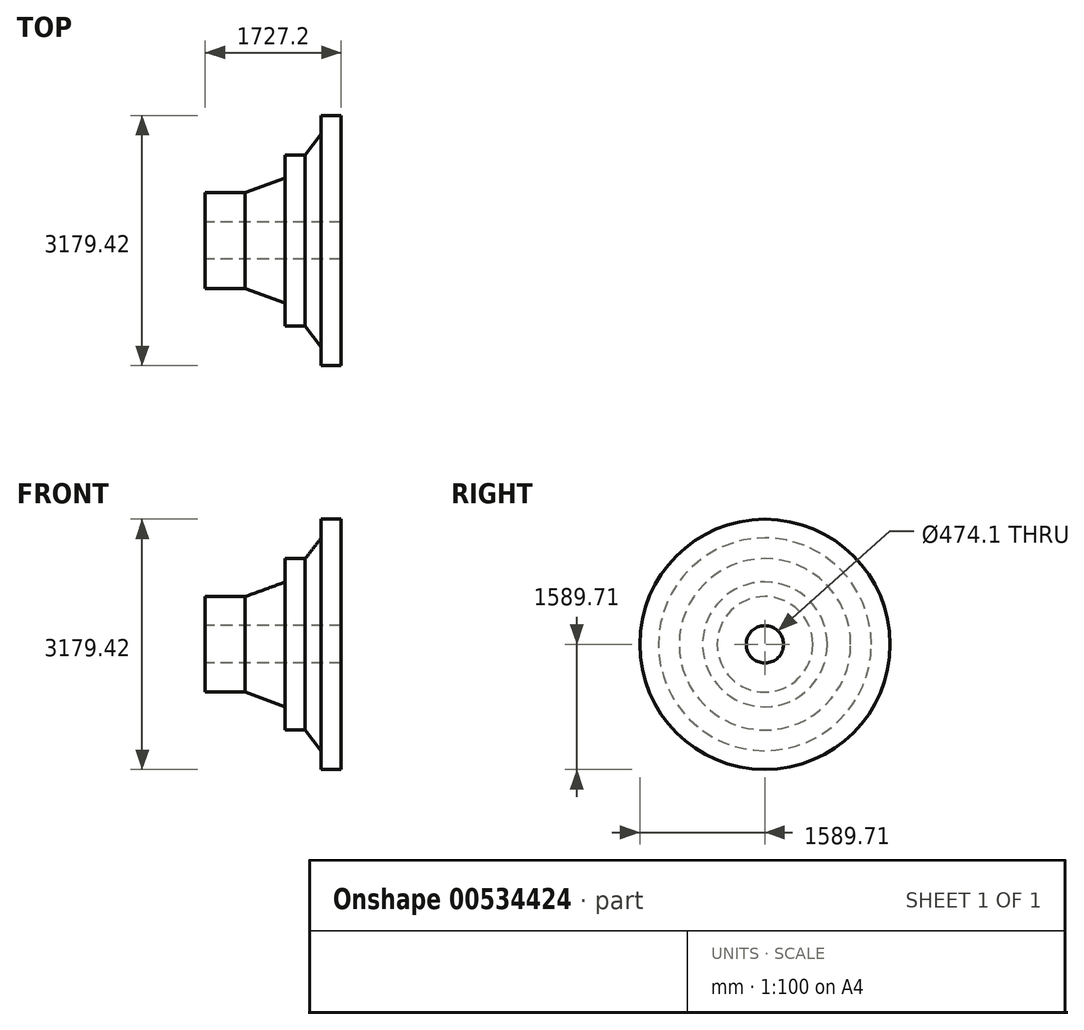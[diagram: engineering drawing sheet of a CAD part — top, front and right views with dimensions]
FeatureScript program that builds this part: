
annotation { "Feature Type Name" : "Feature", "Feature Type Description" : "" }
export const myFeature = defineFeature(function(context is Context, id is Id, definition is map)
    precondition{}
    {
        {
            var Q0;
            Q0=qCreatedBy(makeId("Front.planeOp"),FACE);
            var sketch = newSketch(context, id + "F0", { "sketchPlane" : qUnion([Q0])});
            skLineSegment(sketch, "E0", {"start": v(-1473.2, 0) * mm, "end": v(-1473.2, 369.77) * mm});
            skLineSegment(sketch, "E1", {"start": v(-1473.2, 369.77) * mm, "end": v(-965.2, 369.77) * mm});
            skLineSegment(sketch, "E2", {"start": v(-965.2, 369.77) * mm, "end": v(-457.2, 555.85) * mm});
            skLineSegment(sketch, "E3", {"start": v(-457.2, 555.85) * mm, "end": v(-457.2, 851.67) * mm});
            skLineSegment(sketch, "E4", {"start": v(-457.2, 851.67) * mm, "end": v(-203.2, 851.67) * mm});
            skLineSegment(sketch, "E5", {"start": v(-203.2, 851.67) * mm, "end": v(0, 1114.1) * mm});
            skLineSegment(sketch, "E6", {"start": v(0, 1114.1) * mm, "end": v(0, 1352.66) * mm});
            skLineSegment(sketch, "E7", {"start": v(0, 1352.66) * mm, "end": v(254, 1352.66) * mm});
            skLineSegment(sketch, "E8", {"start": v(254, 1352.66) * mm, "end": v(254, 0) * mm});
            skLineSegment(sketch, "E9", {"start": v(254, 0) * mm, "end": v(-1473.2, 0) * mm});
            skLineSegment(sketch, "E10", {"start": v(-1681.94, -237.05) * mm, "end": v(1643.79, -237.05) * mm});
            skSolve(sketch);
        }
        {
            var Q0;
            Q0=makeQuery(id+"F0.imprint","IMPRINT",FACE,{"disambiguationData":[TD([[makeQuery(id+"F0.imprint","IMPRINT",EDGE,{"derivedFrom":sQuery(id+"F0.wireOp",EDGE,"E0")}),-1.0]])]});
            var Q1;
            Q1=sQuery(id+"F0.wireOp",EDGE,"E10");
            revolve(context, id + "F1", {"entities" : qUnion([Q0]), "axis" : qUnion([Q1]), "revolveType" : RevolveType.FULL});
        }
    });
